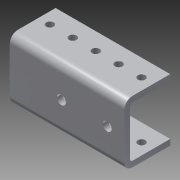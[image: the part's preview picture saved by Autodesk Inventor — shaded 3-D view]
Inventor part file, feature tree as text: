
AUTODESK INVENTOR PART (.ipt)
format: ipt  version: 2014 (Build 180170000, 170)  size: 215,552 bytes
history: native  units: in
note: dims shown in document units (in); Inventor stores cm internally (conversion verified against a paired STEP export)
features: sheet_metal_op x4, other x4, sketch x3, extrude x1
ambient origin geometry x8: Origin, YZ Plane, XZ Plane, XY Plane, X Axis, Y Axis, Z Axis, Center Point
bodies: Solid1 (feature_tree)
feature tree (12):
  sheet_metal_op  "Face1"
  sheet_metal_op  "Flange1"
  extrude  "Extrusion1"  Depth=1.0in
  sketch  "Sketch1"  dims[d0=2.5in d1=1.0in]
  other  "Plate1"
  sketch  "Sketch2"  dims[d2=0.196in]
  other  "Plate2"
  sheet_metal_op  "Bend1"
  sheet_metal_op  "Corner1"
  sketch  "Sketch3"  dims[d3=0.7874in d5=1.0in d6=0.3937in d8=1.0in d10=0.5in d11=1.125in d12=0.125in d13=0.125in d14=0.0625in d15=0.25in d16=0.125in d17=1.0in d18=90.0deg d19=0.05in d20=0.5in d21=0.125in d22=0.125in d23=0.163in d24=0.5in d25=0.25in d26=1.9685in d28=0.5in d29=0.3937in d31=1.0in d33=2.0in d34=0.0in d4=0.125in]
  other  "Definition1"
  other  "Cut1"
